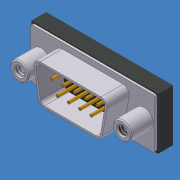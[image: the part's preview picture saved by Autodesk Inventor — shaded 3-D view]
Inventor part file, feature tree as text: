
AUTODESK INVENTOR PART (.ipt)
format: ipt  version: unknown  size: 307,712 bytes
history: native  units: mm (DEFAULTED — no unit token found)
features: sketch x7, extrude x6, mirror x2, hole x1, chamfer x1
ambient origin geometry x8: Origin, YZ Plane, XZ Plane, XY Plane, X Axis, Y Axis, Z Axis, Center Point
feature tree (17):
  extrude  "Extrusion1"  Depth=9.96mm
  extrude  "Extrusion2"  Depth=30.81mm
  extrude  "Extrusion3"  Depth=12.58mm
  extrude  "Extrusion4"  Depth=17.453293mm
  extrude  "Extrusion5"  Depth=1.0mm
  hole  "Hole2"  [1 undecoded]
  chamfer  "Chamfer2"  Distance=0.5mm
  mirror  "Mirror2"
  extrude  "Extrusion6"  Depth=5.9mm TaperAngle=0.0deg
  mirror  "Mirror3"
  sketch  "Sketch1"  dims[d0=16.96mm d1=9.96mm]
  sketch  "Sketch2"  dims[d2=3.6mm d3=30.81mm]
  sketch  "Sketch5"  dims[d4=0.0001mm d5=0.0mm d6=12.58mm]
  sketch  "Sketch6"  dims[d7=3.6mm d8=0.0mm d22=17.453293mm]
  sketch  "Sketch7"  dims[d23=17.453293mm d24=1.0mm]
  sketch  "Sketch8"  dims[d25=1.0mm d26=8.25mm]
  sketch  "Sketch9"  dims[d27=16.79mm d29=0.5mm d30=5.9mm d31=0.0mm d32=0.25mm d33=0.5mm d34=0.5mm d35=0.0mm d36=4.5mm d37=2.91mm d38=5.4mm d39=0.0mm d40=2.156mm d41=6.0mm d42=4.0mm d43=2.0mm d44=14.3117mm d45=8.0mm d46=20.594885mm d47=0.25mm d48=2.0mm d49=2.84mm d50=1.37mm d51=0.67mm d52=30.0mm d54=2.74mm d55=10.0mm d57=10.0mm d59=5.0mm d60=0.0mm d61=45.0deg]
note: 1 required parameter value undecoded (feature->parameter linkage not recoverable at this tier; creation-order binding heuristic only, values carry confidence <= 0.55)
